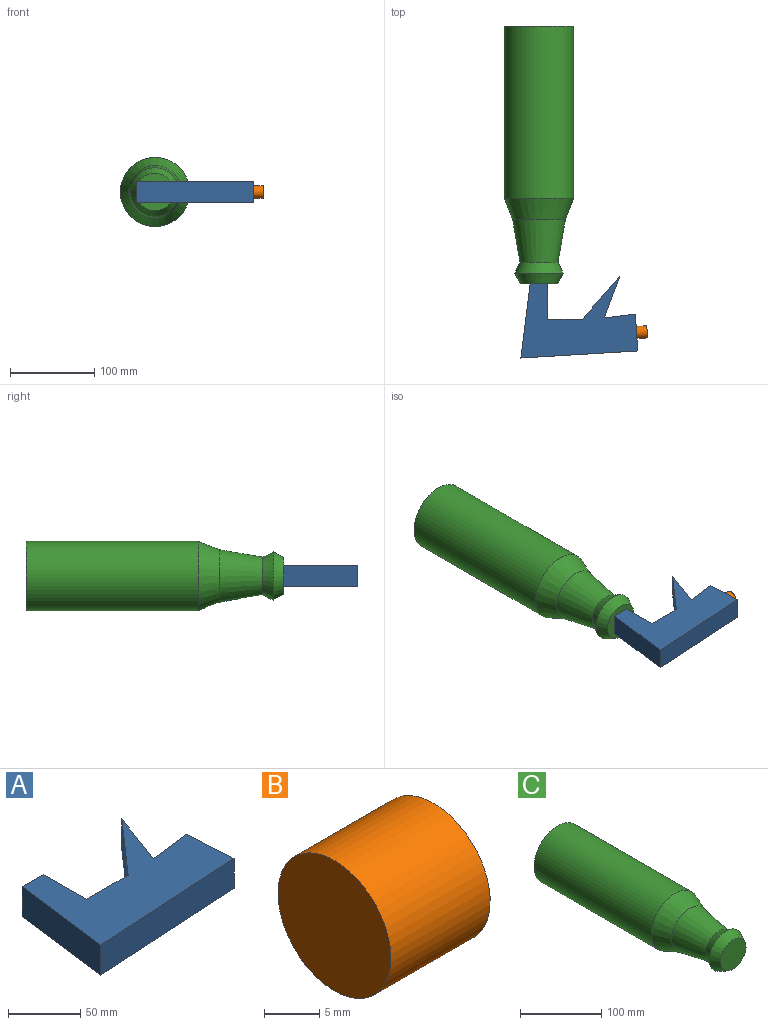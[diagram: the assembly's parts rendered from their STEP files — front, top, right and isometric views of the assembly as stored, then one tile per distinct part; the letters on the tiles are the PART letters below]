
ASSEMBLY  parts=3 mates=2
PART A: 11 faces, bbox 138.5x96.9x25.4 mm
  f0: plane 43.85x25.4mm, normal (1,0.06,0), area 1115.8mm2, adj f1,f8,f9,f10
  f1: plane 36.92x25.4mm, normal (-0.12,0.99,0), area 944.9mm2, adj f0,f2,f9,f10
  f2: plane 49.34x25.4mm, normal (0.94,-0.35,0), area 1337mm2, adj f1,f3,f9,f10
  f3: plane 50.92x44.58mm, normal (-0.75,0.66,0), area 1718.9mm2, adj f2,f4,f9,f10
  f4: plane 40.91x25.4mm, normal (0,1,0), area 1039.2mm2, adj f3,f5,f9,f10
  f5: plane 42.11x25.4mm, normal (1,0,0), area 1069.5mm2, adj f4,f6,f9,f10
  f6: plane 25.4x20.84mm, normal (0,1,0), area 529.3mm2, adj f5,f7,f9,f10
  f7: plane 88.11x25.4mm, normal (-0.99,0.12,0), area 2255.3mm2, adj f6,f8,f9,f10
  f8: plane 138.52x25.4mm, normal (0.06,-1,0), area 3524.7mm2, adj f0,f7,f9,f10
  f9: plane 138.52x96.92mm, normal (0,0,1), area 7406.6mm2, adj f0,f1,f2,f3,f4,f5,f6,f7
  f10: plane 138.52x96.92mm, normal (0,0,-1), area 7406.6mm2, adj f0,f1,f2,f3,f4,f5,f6,f7
PART B: 3 faces, bbox 12.7x14.5x14.5 mm
  f0: cylinder r=7.23mm len=14.45mm, axis (-1,0,0), area 576.7mm2, adj f1,f2
  f1: plane 14.45x14.45mm, normal (1,0,0), area 164.1mm2, adj f0
  f2: plane 14.45x14.45mm, normal (-1,0,0), area 164.1mm2, adj f0
PART C: 7 faces, bbox 82.2x306.1x82.2 mm
  f0: cylinder r=41.12mm len=204.47mm, axis (0,1,0), area 52833.8mm2, adj f1,f2
  f1: plane 82.25x82.25mm, normal (0,1,0), area 5313.2mm2, adj f0
  f2: cone r=31.3mm half-angle=21.1deg, axis (0,1,0), area 6196.5mm2, adj f0,f3
  f3: cone r=31.3mm half-angle=9.8deg, axis (0,1,0), area 8723.2mm2, adj f2,f4
  f4: cone r=22.56mm half-angle=26deg, axis (0,-1,0), area 2278.6mm2, adj f3,f6
  f5: plane 44.49x44.49mm, normal (0,-1,0), area 1554.7mm2, adj f6
  f6: cone r=28.76mm half-angle=27.2deg, axis (0,1,0), area 2287.2mm2, adj f4,f5
PLACE A t=(-234.72,141.19,-133.8)mm
PLACE B rot(axis=(0,0,1),3.4deg) t=(-28.21,-211.18,-68.11)mm
PLACE C t=(-147.09,203.97,-121.1)mm
MATE parallel A.f6 <-> C.f0  axis (0,1,0) through (-147.09,-102.1,-121.1)mm
MATE parallel B.f0 <-> A.f0  axis (-1,-0.06,0) through (-31.29,-159.96,-121.1)mm
